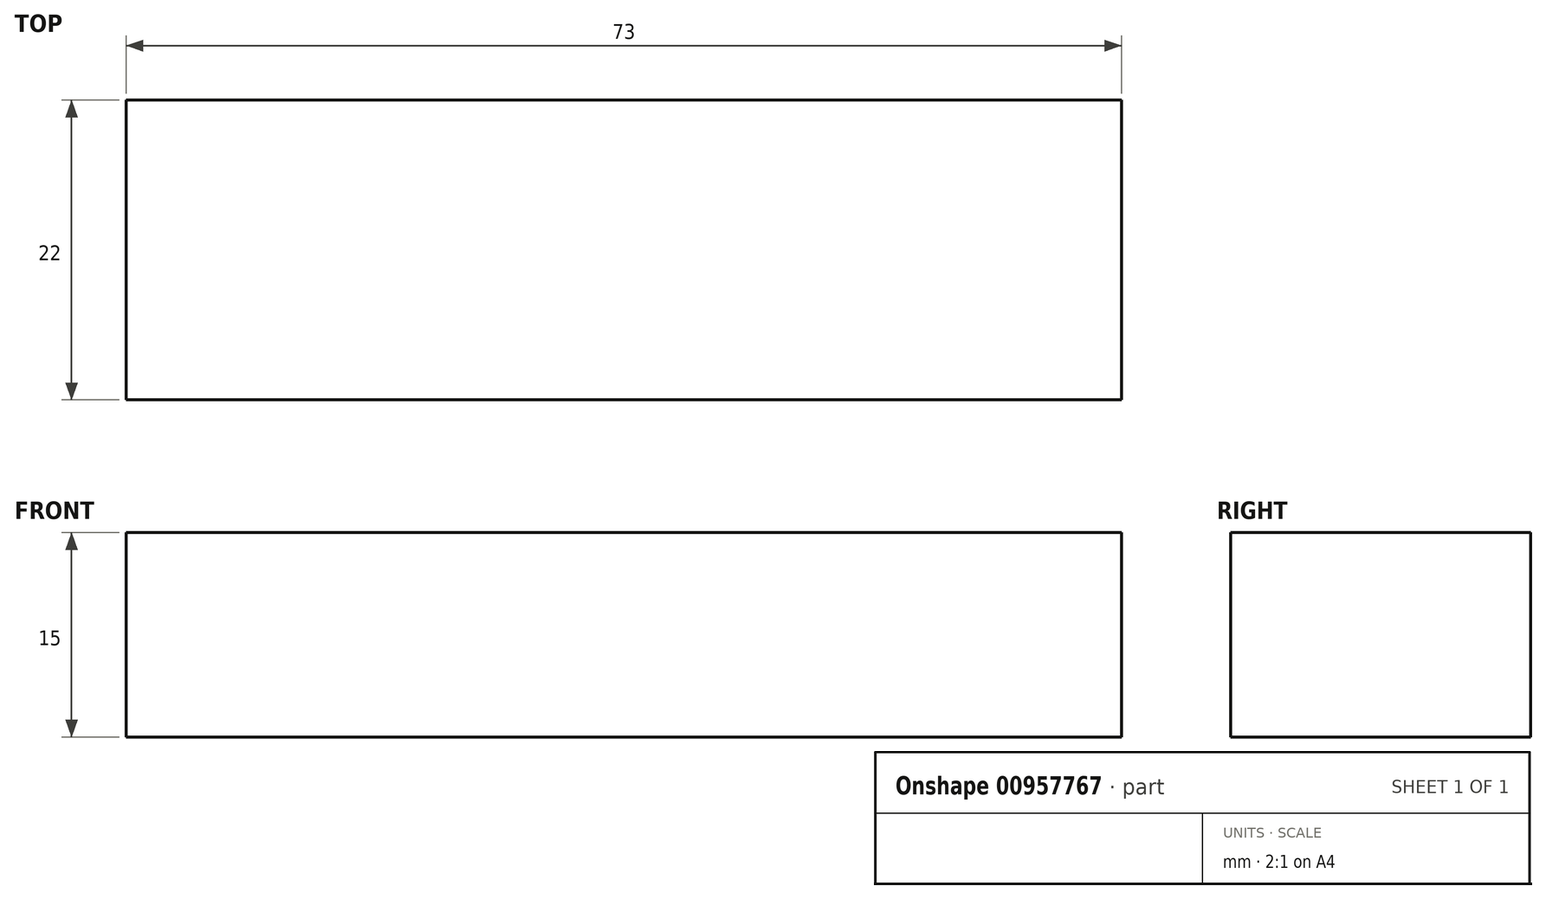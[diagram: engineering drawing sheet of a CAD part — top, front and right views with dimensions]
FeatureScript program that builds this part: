
annotation { "Feature Type Name" : "Feature", "Feature Type Description" : "" }
export const myFeature = defineFeature(function(context is Context, id is Id, definition is map)
    precondition{}
    {
        {
            var Q0;
            Q0=qCreatedBy(makeId("Top.planeOp"),FACE);
            var sketch = newSketch(context, id + "F0", { "sketchPlane" : qUnion([Q0])});
            skLineSegment(sketch, "E0.bottom", {"start": v(-36.5, 11) * mm, "end": v(36.5, 11) * mm});
            skLineSegment(sketch, "E0.top", {"start": v(-36.5, -11) * mm, "end": v(36.5, -11) * mm});
            skLineSegment(sketch, "E0.left", {"start": v(-36.5, 11) * mm, "end": v(-36.5, -11) * mm});
            skLineSegment(sketch, "E0.right", {"start": v(36.5, 11) * mm, "end": v(36.5, -11) * mm});
            skPoint(sketch, "E0.middle", {"position": v(0, 0) * mm});
            skSolve(sketch);
        }
        {
            var Q0;
            Q0=makeQuery(id+"F0.imprint","IMPRINT",FACE,{"disambiguationData":[TD([[makeQuery(id+"F0.imprint","IMPRINT",EDGE,{"derivedFrom":sQuery(id+"F0.wireOp",EDGE,"E0.bottom")}),-1.0]])]});
            extrude(context, id + "F1", {"entities" : qUnion([Q0]), "depth" : 15 * mm, "offsetDistance" : 25 * mm});
        }
    });
